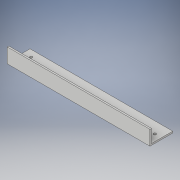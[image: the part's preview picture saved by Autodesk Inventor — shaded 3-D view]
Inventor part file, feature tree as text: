
AUTODESK INVENTOR PART (.ipt)
format: ipt  version: 2018 (Build 220112000, 112)  size: 122,880 bytes
history: native  units: in
note: dims shown in document units (in); Inventor stores cm internally (conversion verified against a paired STEP export)
features: extrude x4, sketch x4
ambient origin geometry x8: Origin, YZ Plane, XZ Plane, XY Plane, X Axis, Y Axis, Z Axis, Center Point
bodies: Solid1 (feature_tree)
feature tree (8):
  extrude  "Extrusion1"  Depth=1.755in
  extrude  "Extrusion2"  Depth=11.0in
  extrude  "Extrusion3"  Depth=1.0in TaperAngle=0.0deg
  extrude  "Extrusion4"  Depth=1.0in
  sketch  "Sketch1"  dims[d0=11.0in d1=1.755in]
  sketch  "Sketch2"  dims[d2=0.125in d3=0.0in d4=11.0in]
  sketch  "Sketch3"  dims[d5=0.125in d6=1.0in d7=0.0in]
  sketch  "Sketch4"  dims[d14=1.0in d15=0.0in d26=0.5in d27=0.875in d28=0.2031in d29=1.0in d30=0.0in]
